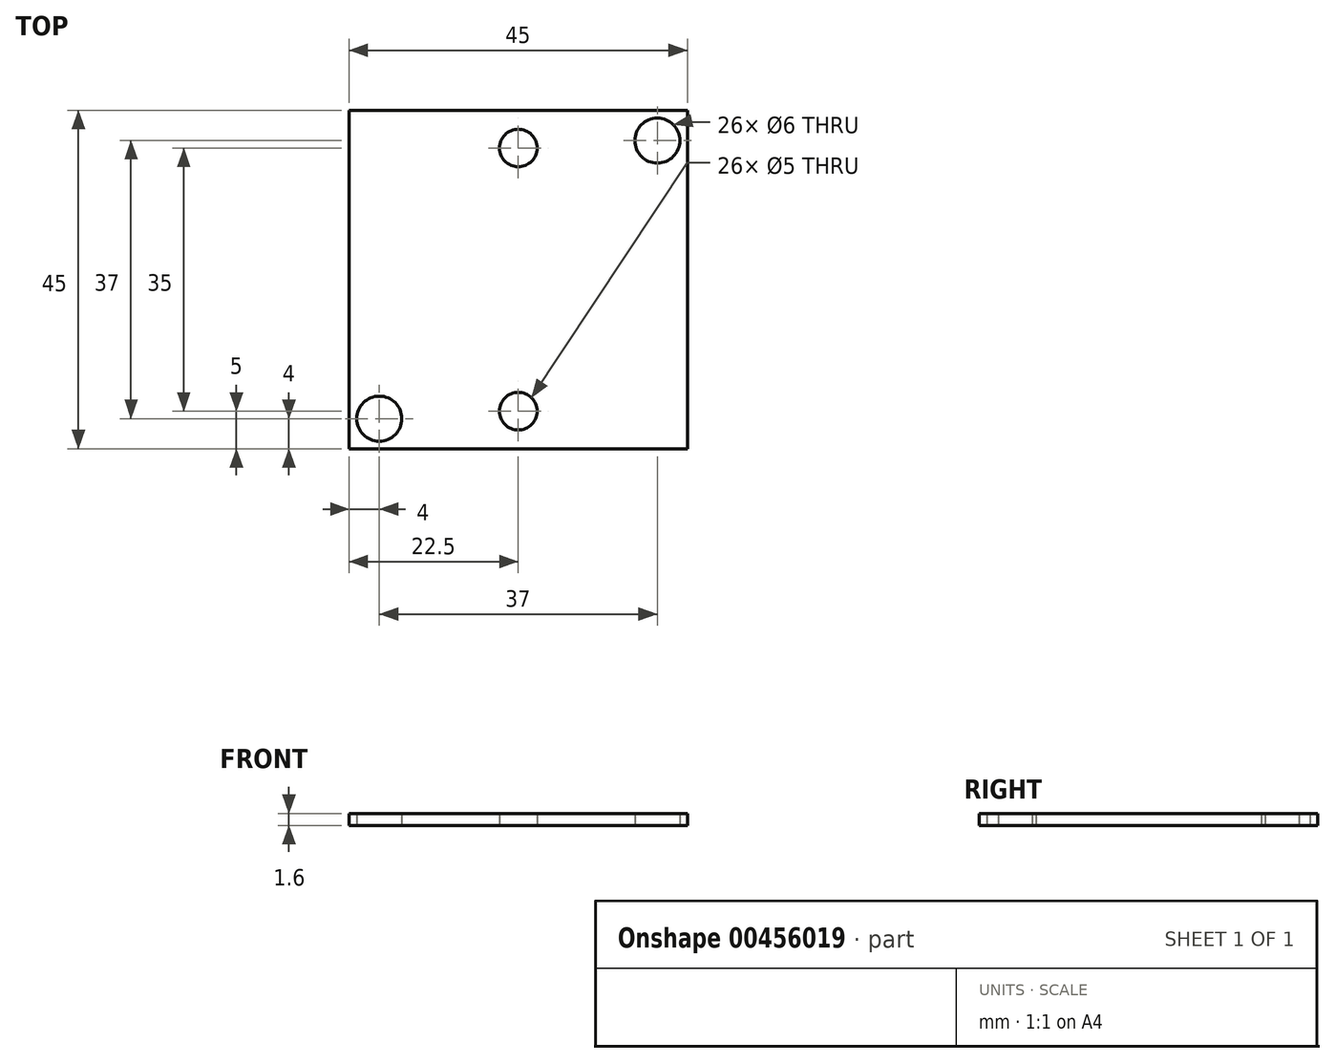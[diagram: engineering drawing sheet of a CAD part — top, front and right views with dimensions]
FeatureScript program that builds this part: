
annotation { "Feature Type Name" : "Feature", "Feature Type Description" : "" }
export const myFeature = defineFeature(function(context is Context, id is Id, definition is map)
    precondition{}
    {
        {
            var Q0;
            Q0=qCreatedBy(makeId("Top.planeOp"),FACE);
            var sketch = newSketch(context, id + "F0", { "sketchPlane" : qUnion([Q0])});
            skLineSegment(sketch, "E0.bottom", {"start": v(22.5, 22.5) * mm, "end": v(-22.5, 22.5) * mm});
            skLineSegment(sketch, "E0.top", {"start": v(22.5, -22.5) * mm, "end": v(-22.5, -22.5) * mm});
            skLineSegment(sketch, "E0.left", {"start": v(22.5, 22.5) * mm, "end": v(22.5, -22.5) * mm});
            skLineSegment(sketch, "E0.right", {"start": v(-22.5, 22.5) * mm, "end": v(-22.5, -22.5) * mm});
            skPoint(sketch, "E0.middle", {"position": v(0, 0) * mm});
            skCircle(sketch, "E1", {"center": v(0, 17.5) * mm, "radius": 2.5 * mm});
            skLineSegment(sketch, "E2", {"start": v(-22.5, 0) * mm, "end": v(22.5, 0) * mm, "construction": true});
            skCircle(sketch, "E3.MirrorC", {"center": v(0, -17.5) * mm, "radius": 2.5 * mm});
            skCircle(sketch, "E4", {"center": v(18.5, 18.5) * mm, "radius": 3 * mm});
            skLineSegment(sketch, "E5", {"start": v(0, 0) * mm, "end": v(22.5, 22.5) * mm, "construction": true});
            skLineSegment(sketch, "E6", {"start": v(-22.5, 22.5) * mm, "end": v(22.5, -22.5) * mm, "construction": true});
            skCircle(sketch, "E7.MirrorC", {"center": v(-18.5, -18.5) * mm, "radius": 3 * mm});
            skSolve(sketch);
        }
        {
            var Q0;
            Q0=makeQuery(id+"F0.imprint","IMPRINT",FACE,{"disambiguationData":[TD([[makeQuery(id+"F0.imprint","IMPRINT",EDGE,{"derivedFrom":sQuery(id+"F0.wireOp",EDGE,"E0.bottom")}),1.0]])]});
            extrude(context, id + "F1", {"entities" : qUnion([Q0]), "depth" : 1.6 * mm});
        }
    });
